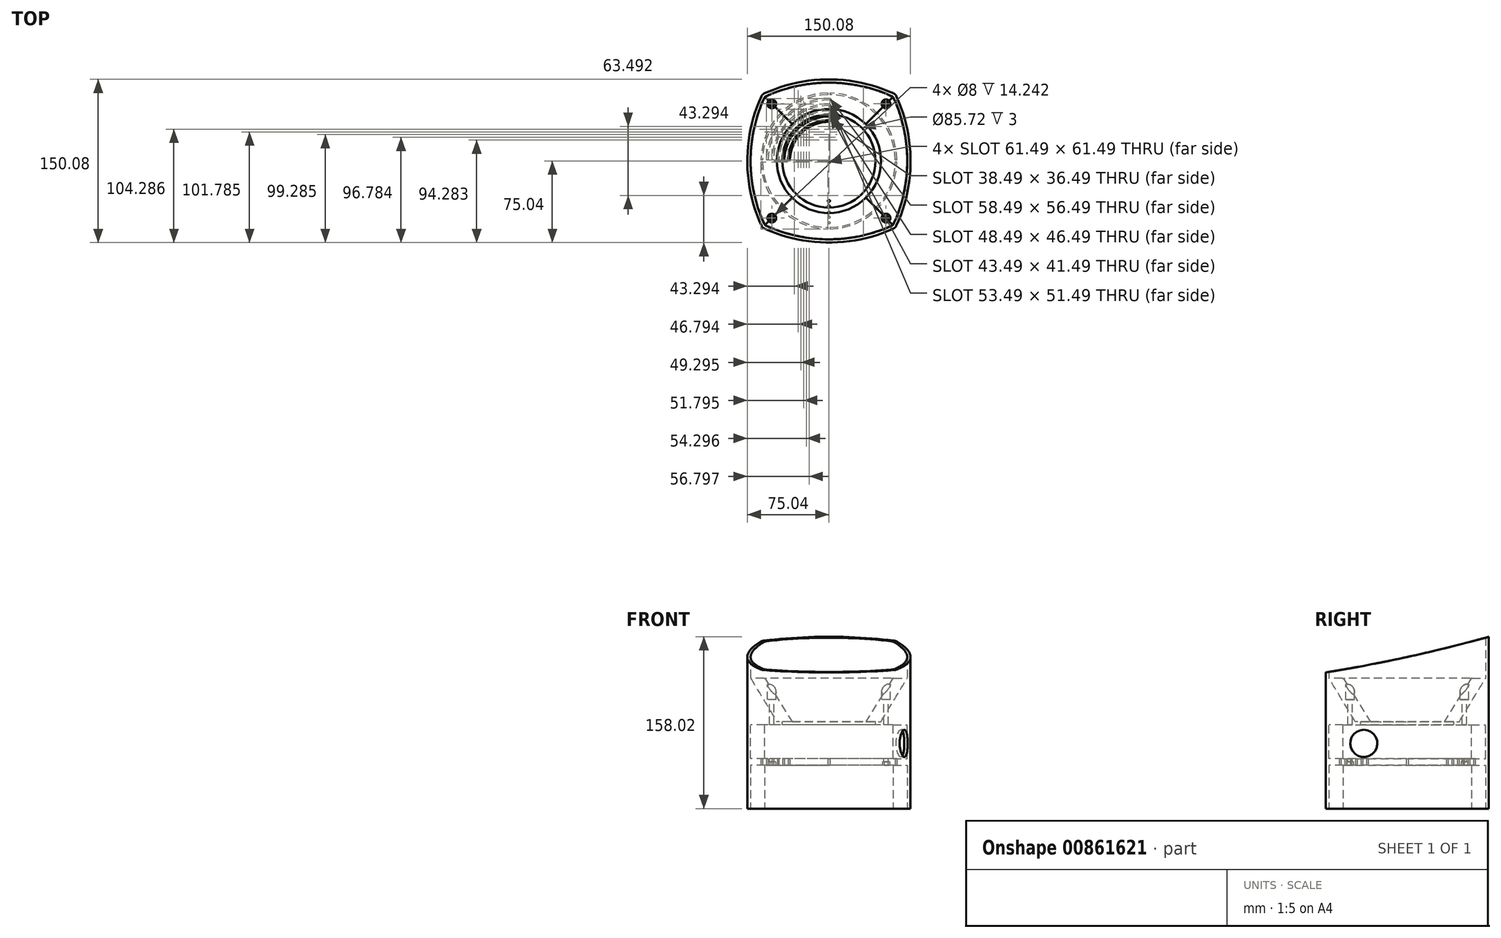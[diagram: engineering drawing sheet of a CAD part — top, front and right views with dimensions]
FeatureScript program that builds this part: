
annotation { "Feature Type Name" : "Feature", "Feature Type Description" : "" }
export const myFeature = defineFeature(function(context is Context, id is Id, definition is map)
    precondition{}
    {
        {
            var Q0;
            Q0=qCreatedBy(makeId("Top.planeOp"),FACE);
            var sketch = newSketch(context, id + "F0", { "sketchPlane" : qUnion([Q0])});
            skLineSegment(sketch, "E0.bottom", {"start": v(196, 49) * mm, "end": v(-196, 49) * mm, "construction": true});
            skLineSegment(sketch, "E0.top", {"start": v(196, -49) * mm, "end": v(-196, -49) * mm, "construction": true});
            skLineSegment(sketch, "E0.left", {"start": v(196, 49) * mm, "end": v(196, -49) * mm, "construction": true});
            skLineSegment(sketch, "E0.right", {"start": v(-196, 49) * mm, "end": v(-196, -49) * mm, "construction": true});
            skPoint(sketch, "E0.middle", {"position": v(0, 0) * mm});
            skLineSegment(sketch, "E1.bottom", {"start": v(207, 59) * mm, "end": v(-207, 59) * mm, "construction": true});
            skLineSegment(sketch, "E1.top", {"start": v(207, -59) * mm, "end": v(-207, -59) * mm, "construction": true});
            skLineSegment(sketch, "E1.left", {"start": v(207, 59) * mm, "end": v(207, -59) * mm, "construction": true});
            skLineSegment(sketch, "E1.right", {"start": v(-207, 59) * mm, "end": v(-207, -59) * mm, "construction": true});
            skLineSegment(sketch, "E2", {"start": v(0, -59) * mm, "end": v(0, 59) * mm, "construction": true});
            skLineSegment(sketch, "E3", {"start": v(-207, 0) * mm, "end": v(207, 0) * mm, "construction": true});
            skCircle(sketch, "E4", {"center": v(0, 0) * mm, "radius": 47.86 * mm});
            skLineSegment(sketch, "E5.bottom", {"start": v(59, 59) * mm, "end": v(-59, 59) * mm, "construction": true});
            skLineSegment(sketch, "E5.top", {"start": v(59, -59) * mm, "end": v(-59, -59) * mm, "construction": true});
            skLineSegment(sketch, "E5.left", {"start": v(59, 59) * mm, "end": v(59, -59) * mm, "construction": true});
            skLineSegment(sketch, "E5.right", {"start": v(-59, 59) * mm, "end": v(-59, -59) * mm, "construction": true});
            skArc(sketch, "E6", {"start": v(59, 59) * mm, "mid": v(0, 72.04) * mm, "end": v(-59, 59) * mm});
            skArc(sketch, "E7", {"start": v(59, -59) * mm, "mid": v(72.04, 0) * mm, "end": v(59, 59) * mm});
            skArc(sketch, "E8", {"start": v(-59, -59) * mm, "mid": v(0, -72.04) * mm, "end": v(59, -59) * mm});
            skArc(sketch, "E9", {"start": v(-59, 59) * mm, "mid": v(-72.04, 0) * mm, "end": v(-59, -59) * mm});
            skArc(sketch, "E10.0", {"start": v(61.26, 61.26) * mm, "mid": v(0, 75.04) * mm, "end": v(-61.26, 61.26) * mm});
            skArc(sketch, "E10.1", {"start": v(61.26, -61.26) * mm, "mid": v(75.04, 0) * mm, "end": v(61.26, 61.26) * mm});
            skArc(sketch, "E10.2", {"start": v(-61.26, -61.26) * mm, "mid": v(0, -75.04) * mm, "end": v(61.26, -61.26) * mm});
            skArc(sketch, "E10.3", {"start": v(-61.26, 61.26) * mm, "mid": v(-75.04, 0) * mm, "end": v(-61.26, -61.26) * mm});
            skSolve(sketch);
        }
        {
            var Q0;
            {var subQ8=sQuery(id+"F0.wireOp",EDGE,"E6");Q0=makeQuery(id+"F0.imprint","IMPRINT",FACE,{"disambiguationData":[TD([[makeQuery(id+"F0.imprint","IMPRINT",EDGE,{"derivedFrom":subQ8}),-1.0]])]});}
            var Q1;
            {var subQ0=sQuery(id+"F0.wireOp",EDGE,"E10.1");var subQ1=sQuery(id+"F0.wireOp",EDGE,"2c3d49d2-39e6-4b7c-b00d-7af9e24e8e71.0");var subQ2=makeQuery(id+"F0.imprint","INTERSECT",VERTEX,{"disambiguationData":[OD(0.0)],"derivedFrom":[subQ1,subQ0]});Q1=makeQuery(id+"F0.imprint","IMPRINT",FACE,{"disambiguationData":[TD([[makeQuery(id+"F0.imprint","IMPRINT",EDGE,{"disambiguationData":[TD([[subQ2,-1.0]])],"derivedFrom":subQ1}),1.0]])]});}
            extrude(context, id + "F1", {"entities" : qUnion([Q0, Q1]), "endBound" : BoundingType.SYMMETRIC, "depth" : 160 * mm, "offsetDistance" : 25 * mm});
        }
        {
            var Q0;
            Q0=qCreatedBy(makeId("Right.planeOp"),FACE);
            var sketch = newSketch(context, id + "F2", { "sketchPlane" : qUnion([Q0])});
            skCircle(sketch, "E11", {"center": v(-294.04, 1407.06) * mm, "radius": 1379.34 * mm});
            skLineSegment(sketch, "E12", {"start": v(0, 0) * mm, "end": v(-237.77, 0) * mm, "construction": true});
            skCircle(sketch, "E13.MirrorC", {"center": v(-294.04, -1407.06) * mm, "radius": 1379.34 * mm});
            skSolve(sketch);
        }
        {
            var Q0;
            Q0=makeQuery(id+"F2.imprint","IMPRINT",FACE,{"disambiguationData":[TD([[makeQuery(id+"F2.imprint","IMPRINT",EDGE,{"derivedFrom":sQuery(id+"F2.wireOp",EDGE,"E11")}),1.0]])]});
            var Q1;
            Q1=makeQuery(id+"F2.imprint","IMPRINT",FACE,{"disambiguationData":[TD([[makeQuery(id+"F2.imprint","IMPRINT",EDGE,{"derivedFrom":sQuery(id+"F2.wireOp",EDGE,"E13.MirrorC")}),-1.0]])]});
            extrude(context, id + "F3", {"entities" : qUnion([Q0, Q1]), "operationType" : NewBodyOperationType.REMOVE, "endBound" : BoundingType.SYMMETRIC, "oppositeDirection" : true, "depth" : 780 * mm, "offsetDistance" : 25 * mm});
        }
        {
            var Q0;
            Q0=qCreatedBy(makeId("Top.planeOp"),FACE);
            cPlane(context, id + "F4", {"entities" : qUnion([Q0]), "cplaneType" : CPlaneType.OFFSET, "offset" : 40 * mm, "width" : 150 * mm, "height" : 150 * mm});
        }
        {
            var Q0;
            Q0=qCreatedBy(id+"F4.planeOp",FACE);
            var sketch = newSketch(context, id + "F5", { "sketchPlane" : qUnion([Q0])});
            skLineSegment(sketch, "E14.bottom", {"start": v(59, 59) * mm, "end": v(-59, 59) * mm, "construction": true});
            skLineSegment(sketch, "E14.top", {"start": v(59, -59) * mm, "end": v(-59, -59) * mm, "construction": true});
            skLineSegment(sketch, "E14.left", {"start": v(59, 59) * mm, "end": v(59, -59) * mm, "construction": true});
            skLineSegment(sketch, "E14.right", {"start": v(-59, 59) * mm, "end": v(-59, -59) * mm, "construction": true});
            skPoint(sketch, "E14.middle", {"position": v(0, 0) * mm});
            skArc(sketch, "E15", {"start": v(59, 59) * mm, "mid": v(0, 72.04) * mm, "end": v(-59, 59) * mm});
            skArc(sketch, "E16", {"start": v(59, -59) * mm, "mid": v(72.04, 0) * mm, "end": v(59, 59) * mm});
            skArc(sketch, "E17", {"start": v(-59, -59) * mm, "mid": v(0, -72.04) * mm, "end": v(59, -59) * mm});
            skArc(sketch, "E18", {"start": v(-59, 59) * mm, "mid": v(-72.04, 0) * mm, "end": v(-59, -59) * mm});
            skSolve(sketch);
        }
        {
            var Q0;
            Q0=qCreatedBy(makeId("Top.planeOp"),FACE);
            var sketch = newSketch(context, id + "F6", { "sketchPlane" : qUnion([Q0])});
            skLineSegment(sketch, "E19.bottom", {"start": v(59, 59) * mm, "end": v(-59, 59) * mm, "construction": true});
            skLineSegment(sketch, "E19.top", {"start": v(59, -59) * mm, "end": v(-59, -59) * mm, "construction": true});
            skLineSegment(sketch, "E19.left", {"start": v(59, 59) * mm, "end": v(59, -59) * mm, "construction": true});
            skLineSegment(sketch, "E19.right", {"start": v(-59, 59) * mm, "end": v(-59, -59) * mm, "construction": true});
            skPoint(sketch, "E19.middle", {"position": v(0, 0) * mm});
            skArc(sketch, "E20", {"start": v(59, 59) * mm, "mid": v(0, 72.04) * mm, "end": v(-59, 59) * mm});
            skArc(sketch, "E21", {"start": v(59, -59) * mm, "mid": v(72.04, 0) * mm, "end": v(59, 59) * mm});
            skArc(sketch, "E22", {"start": v(-59, -59) * mm, "mid": v(0, -72.04) * mm, "end": v(59, -59) * mm});
            skArc(sketch, "E23", {"start": v(-59, 59) * mm, "mid": v(-72.04, 0) * mm, "end": v(-59, -59) * mm});
            skArc(sketch, "E24.0", {"start": v(61.26, 61.26) * mm, "mid": v(0, 75.04) * mm, "end": v(-61.26, 61.26) * mm});
            skArc(sketch, "E24.1", {"start": v(61.26, -61.26) * mm, "mid": v(75.04, 0) * mm, "end": v(61.26, 61.26) * mm});
            skArc(sketch, "E24.2", {"start": v(-61.26, -61.26) * mm, "mid": v(0, -75.04) * mm, "end": v(61.26, -61.26) * mm});
            skArc(sketch, "E24.3", {"start": v(-61.26, 61.26) * mm, "mid": v(-75.04, 0) * mm, "end": v(-61.26, -61.26) * mm});
            skSolve(sketch);
        }
        {
            var Q0;
            Q0 = qSketchRegion(id + "F6", true);
            var Q1;
            Q1=makeQuery(id+"F0.imprint","IMPRINT",FACE,{"disambiguationData":[TD([[makeQuery(id+"F0.imprint","IMPRINT",EDGE,{"derivedFrom":sQuery(id+"F0.wireOp",EDGE,"E4")}),-1.0]])]});
            var Q2;
            Q2=makeQuery(id+"F6.imprint","IMPRINT",FACE,{"disambiguationData":[TD([[makeQuery(id+"F6.imprint","IMPRINT",EDGE,{"derivedFrom":sQuery(id+"F6.wireOp",EDGE,"E20")}),1.0]])]});
            extrude(context, id + "F7", {"entities" : qUnion([Q0, Q1, Q2]), "operationType" : NewBodyOperationType.ADD, "endBound" : BoundingType.SYMMETRIC, "depth" : 80 * mm, "offsetDistance" : 25 * mm});
        }
        {
            var Q0;
            Q0=qCreatedBy(makeId("Top.planeOp"),FACE);
            var sketch = newSketch(context, id + "F8", { "sketchPlane" : qUnion([Q0])});
            skCircle(sketch, "E25", {"center": v(0, 0) * mm, "radius": 47.86 * mm});
            skSolve(sketch);
        }
        {
            var Q1;
            Q1 = qSketchRegion(id + "F5", true);
            var Q2;
            Q2 = qSketchRegion(id + "F8", true);
            loft(context, id + "F9", {"operationType" : NewBodyOperationType.REMOVE, "sheetProfilesArray" : [{ "sheetProfileEntities" : qUnion([Q1]) }, { "sheetProfileEntities" : qUnion([Q2]) }]});
        }
        {
            var Q0;
            Q0=makeQuery(id+"F0.imprint","IMPRINT",FACE,{"disambiguationData":[TD([[makeQuery(id+"F0.imprint","IMPRINT",EDGE,{"derivedFrom":sQuery(id+"F0.wireOp",EDGE,"E4")}),1.0]])]});
            var sketch = newSketch(context, id + "F10", { "sketchPlane" : qUnion([Q0])});
            skCircle(sketch, "E26", {"center": v(0, 0) * mm, "radius": 42.86 * mm});
            skSolve(sketch);
        }
        {
            var Q0;
            Q0=makeQuery(id+"F10.imprint","IMPRINT",FACE,{"disambiguationData":[TD([[makeQuery(id+"F10.imprint","IMPRINT",EDGE,{"derivedFrom":sQuery(id+"F10.wireOp",EDGE,"E26")}),1.0]])]});
            extrude(context, id + "F11", {"entities" : qUnion([Q0]), "operationType" : NewBodyOperationType.REMOVE, "oppositeDirection" : true, "depth" : 3 * mm, "offsetDistance" : 25 * mm});
        }
        {
            var Q0;
            Q0=qCreatedBy(makeId("Top.planeOp"),FACE);
            cPlane(context, id + "F12", {"entities" : qUnion([Q0]), "cplaneType" : CPlaneType.OFFSET, "offset" : 3 * mm, "oppositeDirection" : true, "width" : 150 * mm, "height" : 150 * mm});
        }
        {
            var Q0;
            Q0=qCreatedBy(id+"F12.planeOp",FACE);
            var sketch = newSketch(context, id + "F13", { "sketchPlane" : qUnion([Q0])});
            skLineSegment(sketch, "E27.bottom", {"start": v(59, 59) * mm, "end": v(-59, 59) * mm, "construction": true});
            skLineSegment(sketch, "E27.top", {"start": v(59, -59) * mm, "end": v(-59, -59) * mm, "construction": true});
            skLineSegment(sketch, "E27.left", {"start": v(59, 59) * mm, "end": v(59, -59) * mm, "construction": true});
            skLineSegment(sketch, "E27.right", {"start": v(-59, 59) * mm, "end": v(-59, -59) * mm, "construction": true});
            skPoint(sketch, "E27.middle", {"position": v(0, 0) * mm});
            skArc(sketch, "E28", {"start": v(59, 59) * mm, "mid": v(0, 72.04) * mm, "end": v(-59, 59) * mm});
            skArc(sketch, "E29", {"start": v(59, -59) * mm, "mid": v(72.04, 0) * mm, "end": v(59, 59) * mm});
            skArc(sketch, "E30", {"start": v(-59, -59) * mm, "mid": v(0, -72.04) * mm, "end": v(59, -59) * mm});
            skArc(sketch, "E31", {"start": v(-59, 59) * mm, "mid": v(-72.04, 0) * mm, "end": v(-59, -59) * mm});
            skSolve(sketch);
        }
        {
            var Q0;
            Q0 = qSketchRegion(id + "F13", true);
            extrude(context, id + "F14", {"entities" : qUnion([Q0]), "operationType" : NewBodyOperationType.REMOVE, "oppositeDirection" : true, "depth" : 31 * mm, "offsetDistance" : 25 * mm});
        }
        {
            var Q0;
            Q0=makeQuery(id+"F7.boolean.opBoolean","MERGE",FACE,{"derivedFrom":[makeQuery(id+"F7.opExtrude","CAP_FACE",FACE,{"disambiguationData":[OSD([sQuery(id+"F0.wireOp",EDGE,"E4"),sQuery(id+"F0.wireOp",EDGE,"E6"),sQuery(id+"F0.wireOp",EDGE,"E7"),sQuery(id+"F0.wireOp",EDGE,"E8"),sQuery(id+"F0.wireOp",EDGE,"E9")])],"isStart":true}),makeQuery(id+"F7.opExtrude","CAP_FACE",FACE,{"disambiguationData":[OSD([sQuery(id+"F6.wireOp",EDGE,"E24.0"),sQuery(id+"F6.wireOp",EDGE,"E24.1"),sQuery(id+"F6.wireOp",EDGE,"E24.2"),sQuery(id+"F6.wireOp",EDGE,"E24.3")])],"isStart":true})]});
            var sketch = newSketch(context, id + "F15", { "sketchPlane" : qUnion([Q0])});
            skCircle(sketch, "E32", {"center": v(0, 0) * mm, "radius": 62.5 * mm});
            skCircle(sketch, "E33", {"center": v(0, 0) * mm, "radius": 61 * mm});
            skCircle(sketch, "E34", {"center": v(0, 0) * mm, "radius": 57.5 * mm});
            skCircle(sketch, "E35", {"center": v(0, 0) * mm, "radius": 56 * mm});
            skCircle(sketch, "E36", {"center": v(0, 0) * mm, "radius": 52.5 * mm});
            skCircle(sketch, "E37", {"center": v(0, 0) * mm, "radius": 51 * mm});
            skCircle(sketch, "E38", {"center": v(0, 0) * mm, "radius": 47.5 * mm});
            skCircle(sketch, "E39", {"center": v(0, 0) * mm, "radius": 46 * mm});
            skCircle(sketch, "E40", {"center": v(0, 0) * mm, "radius": 42.5 * mm});
            skCircle(sketch, "E41", {"center": v(0, 0) * mm, "radius": 41 * mm});
            skCircle(sketch, "E42", {"center": v(0, 0) * mm, "radius": 37.5 * mm});
            skCircle(sketch, "E43", {"center": v(0, 0) * mm, "radius": 36 * mm});
            skLineSegment(sketch, "E44.bottom", {"start": v(1, -67) * mm, "end": v(-1, -67) * mm});
            skLineSegment(sketch, "E44.top", {"start": v(1, 67) * mm, "end": v(-1, 67) * mm});
            skLineSegment(sketch, "E44.left", {"start": v(1, -67) * mm, "end": v(1, 67) * mm});
            skLineSegment(sketch, "E44.right", {"start": v(-1, -67) * mm, "end": v(-1, 67) * mm});
            skLineSegment(sketch, "E45.bottom", {"start": v(67.5, -1) * mm, "end": v(-67.5, -1) * mm});
            skLineSegment(sketch, "E45.top", {"start": v(67.5, 1) * mm, "end": v(-67.5, 1) * mm});
            skLineSegment(sketch, "E45.left", {"start": v(67.5, -1) * mm, "end": v(67.5, 1) * mm});
            skLineSegment(sketch, "E45.right", {"start": v(-67.5, -1) * mm, "end": v(-67.5, 1) * mm});
            skSolve(sketch);
        }
        {
            var Q0;
            {var subQ0=sQuery(id+"F15.wireOp",EDGE,"E44.right");var subQ1=sQuery(id+"F15.wireOp",EDGE,"E32");var subQ2=makeQuery(id+"F15.imprint","INTERSECT",VERTEX,{"disambiguationData":[OD(0.0)],"derivedFrom":[subQ1,subQ0]});Q0=makeQuery(id+"F15.imprint","IMPRINT",FACE,{"disambiguationData":[TD([[makeQuery(id+"F15.imprint","IMPRINT",EDGE,{"disambiguationData":[TD([[subQ2,-1.0]])],"derivedFrom":subQ1}),1.0]])]});}
            var Q1;
            {var subQ0=sQuery(id+"F15.wireOp",EDGE,"E44.right");var subQ1=sQuery(id+"F15.wireOp",EDGE,"E34");var subQ2=makeQuery(id+"F15.imprint","INTERSECT",VERTEX,{"disambiguationData":[OD(0.0)],"derivedFrom":[subQ1,subQ0]});Q1=makeQuery(id+"F15.imprint","IMPRINT",FACE,{"disambiguationData":[TD([[makeQuery(id+"F15.imprint","IMPRINT",EDGE,{"disambiguationData":[TD([[subQ2,-1.0]])],"derivedFrom":subQ1}),1.0]])]});}
            var Q2;
            {var subQ0=sQuery(id+"F15.wireOp",EDGE,"E44.right");var subQ1=sQuery(id+"F15.wireOp",EDGE,"E36");var subQ2=makeQuery(id+"F15.imprint","INTERSECT",VERTEX,{"disambiguationData":[OD(0.0)],"derivedFrom":[subQ1,subQ0]});Q2=makeQuery(id+"F15.imprint","IMPRINT",FACE,{"disambiguationData":[TD([[makeQuery(id+"F15.imprint","IMPRINT",EDGE,{"disambiguationData":[TD([[subQ2,-1.0]])],"derivedFrom":subQ1}),1.0]])]});}
            var Q3;
            {var subQ0=sQuery(id+"F15.wireOp",EDGE,"E44.right");var subQ1=sQuery(id+"F15.wireOp",EDGE,"E38");var subQ2=makeQuery(id+"F15.imprint","INTERSECT",VERTEX,{"disambiguationData":[OD(0.0)],"derivedFrom":[subQ1,subQ0]});Q3=makeQuery(id+"F15.imprint","IMPRINT",FACE,{"disambiguationData":[TD([[makeQuery(id+"F15.imprint","IMPRINT",EDGE,{"disambiguationData":[TD([[subQ2,-1.0]])],"derivedFrom":subQ1}),1.0]])]});}
            var Q4;
            {var subQ0=sQuery(id+"F15.wireOp",EDGE,"E44.right");var subQ1=sQuery(id+"F15.wireOp",EDGE,"E40");var subQ2=makeQuery(id+"F15.imprint","INTERSECT",VERTEX,{"disambiguationData":[OD(0.0)],"derivedFrom":[subQ1,subQ0]});Q4=makeQuery(id+"F15.imprint","IMPRINT",FACE,{"disambiguationData":[TD([[makeQuery(id+"F15.imprint","IMPRINT",EDGE,{"disambiguationData":[TD([[subQ2,-1.0]])],"derivedFrom":subQ1}),1.0]])]});}
            var Q5;
            {var subQ0=sQuery(id+"F15.wireOp",EDGE,"E44.right");var subQ1=sQuery(id+"F15.wireOp",EDGE,"E42");var subQ2=makeQuery(id+"F15.imprint","INTERSECT",VERTEX,{"disambiguationData":[OD(0.0)],"derivedFrom":[subQ1,subQ0]});Q5=makeQuery(id+"F15.imprint","IMPRINT",FACE,{"disambiguationData":[TD([[makeQuery(id+"F15.imprint","IMPRINT",EDGE,{"disambiguationData":[TD([[subQ2,-1.0]])],"derivedFrom":subQ1}),1.0]])]});}
            var Q6;
            {var subQ0=sQuery(id+"F15.wireOp",EDGE,"E44.left");var subQ1=sQuery(id+"F15.wireOp",EDGE,"E42");var subQ2=makeQuery(id+"F15.imprint","INTERSECT",VERTEX,{"disambiguationData":[OD(0.0)],"derivedFrom":[subQ1,subQ0]});Q6=makeQuery(id+"F15.imprint","IMPRINT",FACE,{"disambiguationData":[TD([[makeQuery(id+"F15.imprint","IMPRINT",EDGE,{"disambiguationData":[TD([[subQ2,1.0]])],"derivedFrom":subQ1}),1.0]])]});}
            var Q7;
            {var subQ0=sQuery(id+"F15.wireOp",EDGE,"E44.left");var subQ1=sQuery(id+"F15.wireOp",EDGE,"E40");var subQ2=makeQuery(id+"F15.imprint","INTERSECT",VERTEX,{"disambiguationData":[OD(0.0)],"derivedFrom":[subQ1,subQ0]});Q7=makeQuery(id+"F15.imprint","IMPRINT",FACE,{"disambiguationData":[TD([[makeQuery(id+"F15.imprint","IMPRINT",EDGE,{"disambiguationData":[TD([[subQ2,1.0]])],"derivedFrom":subQ1}),1.0]])]});}
            var Q8;
            {var subQ0=sQuery(id+"F15.wireOp",EDGE,"E44.left");var subQ1=sQuery(id+"F15.wireOp",EDGE,"E38");var subQ2=makeQuery(id+"F15.imprint","INTERSECT",VERTEX,{"disambiguationData":[OD(0.0)],"derivedFrom":[subQ1,subQ0]});Q8=makeQuery(id+"F15.imprint","IMPRINT",FACE,{"disambiguationData":[TD([[makeQuery(id+"F15.imprint","IMPRINT",EDGE,{"disambiguationData":[TD([[subQ2,1.0]])],"derivedFrom":subQ1}),1.0]])]});}
            var Q9;
            {var subQ0=sQuery(id+"F15.wireOp",EDGE,"E44.left");var subQ1=sQuery(id+"F15.wireOp",EDGE,"E36");var subQ2=makeQuery(id+"F15.imprint","INTERSECT",VERTEX,{"disambiguationData":[OD(0.0)],"derivedFrom":[subQ1,subQ0]});Q9=makeQuery(id+"F15.imprint","IMPRINT",FACE,{"disambiguationData":[TD([[makeQuery(id+"F15.imprint","IMPRINT",EDGE,{"disambiguationData":[TD([[subQ2,1.0]])],"derivedFrom":subQ1}),1.0]])]});}
            var Q10;
            {var subQ0=sQuery(id+"F15.wireOp",EDGE,"E44.left");var subQ1=sQuery(id+"F15.wireOp",EDGE,"E34");var subQ2=makeQuery(id+"F15.imprint","INTERSECT",VERTEX,{"disambiguationData":[OD(0.0)],"derivedFrom":[subQ1,subQ0]});Q10=makeQuery(id+"F15.imprint","IMPRINT",FACE,{"disambiguationData":[TD([[makeQuery(id+"F15.imprint","IMPRINT",EDGE,{"disambiguationData":[TD([[subQ2,1.0]])],"derivedFrom":subQ1}),1.0]])]});}
            var Q11;
            {var subQ0=sQuery(id+"F15.wireOp",EDGE,"E44.left");var subQ1=sQuery(id+"F15.wireOp",EDGE,"E32");var subQ2=makeQuery(id+"F15.imprint","INTERSECT",VERTEX,{"disambiguationData":[OD(0.0)],"derivedFrom":[subQ1,subQ0]});Q11=makeQuery(id+"F15.imprint","IMPRINT",FACE,{"disambiguationData":[TD([[makeQuery(id+"F15.imprint","IMPRINT",EDGE,{"disambiguationData":[TD([[subQ2,1.0]])],"derivedFrom":subQ1}),1.0]])]});}
            var Q12;
            {var subQ0=sQuery(id+"F15.wireOp",EDGE,"E44.left");var subQ1=sQuery(id+"F15.wireOp",EDGE,"E42");var subQ2=makeQuery(id+"F15.imprint","INTERSECT",VERTEX,{"disambiguationData":[OD(1.0)],"derivedFrom":[subQ1,subQ0]});Q12=makeQuery(id+"F15.imprint","IMPRINT",FACE,{"disambiguationData":[TD([[makeQuery(id+"F15.imprint","IMPRINT",EDGE,{"disambiguationData":[TD([[subQ2,-1.0]])],"derivedFrom":subQ1}),1.0]])]});}
            var Q13;
            {var subQ0=sQuery(id+"F15.wireOp",EDGE,"E45.bottom");var subQ1=sQuery(id+"F15.wireOp",EDGE,"E42");var subQ2=makeQuery(id+"F15.imprint","INTERSECT",VERTEX,{"disambiguationData":[OD(0.0)],"derivedFrom":[subQ1,subQ0]});Q13=makeQuery(id+"F15.imprint","IMPRINT",FACE,{"disambiguationData":[TD([[makeQuery(id+"F15.imprint","IMPRINT",EDGE,{"disambiguationData":[TD([[subQ2,-1.0]])],"derivedFrom":subQ1}),1.0]])]});}
            var Q14;
            {var subQ0=sQuery(id+"F15.wireOp",EDGE,"E45.bottom");var subQ1=sQuery(id+"F15.wireOp",EDGE,"E40");var subQ2=makeQuery(id+"F15.imprint","INTERSECT",VERTEX,{"disambiguationData":[OD(0.0)],"derivedFrom":[subQ1,subQ0]});Q14=makeQuery(id+"F15.imprint","IMPRINT",FACE,{"disambiguationData":[TD([[makeQuery(id+"F15.imprint","IMPRINT",EDGE,{"disambiguationData":[TD([[subQ2,-1.0]])],"derivedFrom":subQ1}),1.0]])]});}
            var Q15;
            {var subQ0=sQuery(id+"F15.wireOp",EDGE,"E44.left");var subQ1=sQuery(id+"F15.wireOp",EDGE,"E40");var subQ2=makeQuery(id+"F15.imprint","INTERSECT",VERTEX,{"disambiguationData":[OD(1.0)],"derivedFrom":[subQ1,subQ0]});Q15=makeQuery(id+"F15.imprint","IMPRINT",FACE,{"disambiguationData":[TD([[makeQuery(id+"F15.imprint","IMPRINT",EDGE,{"disambiguationData":[TD([[subQ2,-1.0]])],"derivedFrom":subQ1}),1.0]])]});}
            var Q16;
            {var subQ0=sQuery(id+"F15.wireOp",EDGE,"E44.left");var subQ1=sQuery(id+"F15.wireOp",EDGE,"E38");var subQ2=makeQuery(id+"F15.imprint","INTERSECT",VERTEX,{"disambiguationData":[OD(1.0)],"derivedFrom":[subQ1,subQ0]});Q16=makeQuery(id+"F15.imprint","IMPRINT",FACE,{"disambiguationData":[TD([[makeQuery(id+"F15.imprint","IMPRINT",EDGE,{"disambiguationData":[TD([[subQ2,-1.0]])],"derivedFrom":subQ1}),1.0]])]});}
            var Q17;
            {var subQ0=sQuery(id+"F15.wireOp",EDGE,"E45.bottom");var subQ1=sQuery(id+"F15.wireOp",EDGE,"E38");var subQ2=makeQuery(id+"F15.imprint","INTERSECT",VERTEX,{"disambiguationData":[OD(0.0)],"derivedFrom":[subQ1,subQ0]});Q17=makeQuery(id+"F15.imprint","IMPRINT",FACE,{"disambiguationData":[TD([[makeQuery(id+"F15.imprint","IMPRINT",EDGE,{"disambiguationData":[TD([[subQ2,-1.0]])],"derivedFrom":subQ1}),1.0]])]});}
            var Q18;
            {var subQ0=sQuery(id+"F15.wireOp",EDGE,"E45.bottom");var subQ1=sQuery(id+"F15.wireOp",EDGE,"E36");var subQ2=makeQuery(id+"F15.imprint","INTERSECT",VERTEX,{"disambiguationData":[OD(0.0)],"derivedFrom":[subQ1,subQ0]});Q18=makeQuery(id+"F15.imprint","IMPRINT",FACE,{"disambiguationData":[TD([[makeQuery(id+"F15.imprint","IMPRINT",EDGE,{"disambiguationData":[TD([[subQ2,-1.0]])],"derivedFrom":subQ1}),1.0]])]});}
            var Q19;
            {var subQ0=sQuery(id+"F15.wireOp",EDGE,"E44.left");var subQ1=sQuery(id+"F15.wireOp",EDGE,"E36");var subQ2=makeQuery(id+"F15.imprint","INTERSECT",VERTEX,{"disambiguationData":[OD(1.0)],"derivedFrom":[subQ1,subQ0]});Q19=makeQuery(id+"F15.imprint","IMPRINT",FACE,{"disambiguationData":[TD([[makeQuery(id+"F15.imprint","IMPRINT",EDGE,{"disambiguationData":[TD([[subQ2,-1.0]])],"derivedFrom":subQ1}),1.0]])]});}
            var Q20;
            {var subQ0=sQuery(id+"F15.wireOp",EDGE,"E44.left");var subQ1=sQuery(id+"F15.wireOp",EDGE,"E34");var subQ2=makeQuery(id+"F15.imprint","INTERSECT",VERTEX,{"disambiguationData":[OD(1.0)],"derivedFrom":[subQ1,subQ0]});Q20=makeQuery(id+"F15.imprint","IMPRINT",FACE,{"disambiguationData":[TD([[makeQuery(id+"F15.imprint","IMPRINT",EDGE,{"disambiguationData":[TD([[subQ2,-1.0]])],"derivedFrom":subQ1}),1.0]])]});}
            var Q21;
            {var subQ0=sQuery(id+"F15.wireOp",EDGE,"E45.bottom");var subQ1=sQuery(id+"F15.wireOp",EDGE,"E34");var subQ2=makeQuery(id+"F15.imprint","INTERSECT",VERTEX,{"disambiguationData":[OD(0.0)],"derivedFrom":[subQ1,subQ0]});Q21=makeQuery(id+"F15.imprint","IMPRINT",FACE,{"disambiguationData":[TD([[makeQuery(id+"F15.imprint","IMPRINT",EDGE,{"disambiguationData":[TD([[subQ2,-1.0]])],"derivedFrom":subQ1}),1.0]])]});}
            var Q22;
            {var subQ0=sQuery(id+"F15.wireOp",EDGE,"E45.bottom");var subQ1=sQuery(id+"F15.wireOp",EDGE,"E32");var subQ2=makeQuery(id+"F15.imprint","INTERSECT",VERTEX,{"disambiguationData":[OD(0.0)],"derivedFrom":[subQ1,subQ0]});Q22=makeQuery(id+"F15.imprint","IMPRINT",FACE,{"disambiguationData":[TD([[makeQuery(id+"F15.imprint","IMPRINT",EDGE,{"disambiguationData":[TD([[subQ2,-1.0]])],"derivedFrom":subQ1}),1.0]])]});}
            var Q23;
            {var subQ0=sQuery(id+"F15.wireOp",EDGE,"E44.left");var subQ1=sQuery(id+"F15.wireOp",EDGE,"E32");var subQ2=makeQuery(id+"F15.imprint","INTERSECT",VERTEX,{"disambiguationData":[OD(1.0)],"derivedFrom":[subQ1,subQ0]});Q23=makeQuery(id+"F15.imprint","IMPRINT",FACE,{"disambiguationData":[TD([[makeQuery(id+"F15.imprint","IMPRINT",EDGE,{"disambiguationData":[TD([[subQ2,-1.0]])],"derivedFrom":subQ1}),1.0]])]});}
            extrude(context, id + "F16", {"entities" : qUnion([Q0, Q1, Q2, Q3, Q4, Q5, Q6, Q7, Q8, Q9, Q10, Q11, Q12, Q13, Q14, Q15, Q16, Q17, Q18, Q19, Q20, Q21, Q22, Q23]), "operationType" : NewBodyOperationType.REMOVE, "oppositeDirection" : true, "depth" : 25 * mm, "offsetDistance" : 25 * mm});
        }
        {
            var Q0;
            Q0=makeQuery(id+"F1.opExtrude","SWEPT_EDGE",EDGE,{"disambiguationData":[OSD([sQuery(id+"F0.wireOp",EDGE,"E10.0"),sQuery(id+"F0.wireOp",EDGE,"E10.3")])]});
            var Q1;
            Q1=makeQuery(id+"F1.opExtrude","SWEPT_EDGE",EDGE,{"disambiguationData":[OSD([sQuery(id+"F0.wireOp",EDGE,"E10.2"),sQuery(id+"F0.wireOp",EDGE,"E10.3")])]});
            var Q2;
            Q2=makeQuery(id+"F1.opExtrude","SWEPT_EDGE",EDGE,{"disambiguationData":[OSD([sQuery(id+"F0.wireOp",EDGE,"E10.0"),sQuery(id+"F0.wireOp",EDGE,"E10.1")])]});
            var Q3;
            Q3=makeQuery(id+"F1.opExtrude","SWEPT_EDGE",EDGE,{"disambiguationData":[OSD([sQuery(id+"F0.wireOp",EDGE,"E10.1"),sQuery(id+"F0.wireOp",EDGE,"E10.2")])]});
            var Q4;
            {var subQ0=sQuery(id+"F0.wireOp",EDGE,"E9");var subQ1=sQuery(id+"F0.wireOp",EDGE,"E6");Q4=makeQuery(id+"F7.boolean.opBoolean","SPLIT",EDGE,{"disambiguationData":[TD([makeQuery(id+"F3.boolean.opBoolean","COPY",FACE,{"derivedFrom":makeQuery(id+"F3.opExtrude","SWEPT_FACE",FACE,{"disambiguationData":[OSD([sQuery(id+"F2.wireOp",EDGE,"E11")])]})})])],"derivedFrom":makeQuery(id+"F1.opExtrude","SWEPT_EDGE",EDGE,{"disambiguationData":[OSD([subQ1,subQ0])]})});}
            var Q5;
            {var subQ0=sQuery(id+"F0.wireOp",EDGE,"E7");var subQ1=sQuery(id+"F0.wireOp",EDGE,"E6");Q5=makeQuery(id+"F7.boolean.opBoolean","SPLIT",EDGE,{"disambiguationData":[TD([makeQuery(id+"F3.boolean.opBoolean","COPY",FACE,{"derivedFrom":makeQuery(id+"F3.opExtrude","SWEPT_FACE",FACE,{"disambiguationData":[OSD([sQuery(id+"F2.wireOp",EDGE,"E11")])]})})])],"derivedFrom":makeQuery(id+"F1.opExtrude","SWEPT_EDGE",EDGE,{"disambiguationData":[OSD([subQ1,subQ0])]})});}
            var Q6;
            {var subQ0=sQuery(id+"F0.wireOp",EDGE,"E9");var subQ1=sQuery(id+"F0.wireOp",EDGE,"E8");Q6=makeQuery(id+"F7.boolean.opBoolean","SPLIT",EDGE,{"disambiguationData":[TD([makeQuery(id+"F3.boolean.opBoolean","COPY",FACE,{"derivedFrom":makeQuery(id+"F3.opExtrude","SWEPT_FACE",FACE,{"disambiguationData":[OSD([sQuery(id+"F2.wireOp",EDGE,"E11")])]})})])],"derivedFrom":makeQuery(id+"F1.opExtrude","SWEPT_EDGE",EDGE,{"disambiguationData":[OSD([subQ1,subQ0])]})});}
            var Q7;
            {var subQ0=sQuery(id+"F0.wireOp",EDGE,"E8");var subQ1=sQuery(id+"F0.wireOp",EDGE,"E7");Q7=makeQuery(id+"F7.boolean.opBoolean","SPLIT",EDGE,{"disambiguationData":[TD([makeQuery(id+"F3.boolean.opBoolean","COPY",FACE,{"derivedFrom":makeQuery(id+"F3.opExtrude","SWEPT_FACE",FACE,{"disambiguationData":[OSD([sQuery(id+"F2.wireOp",EDGE,"E11")])]})})])],"derivedFrom":makeQuery(id+"F1.opExtrude","SWEPT_EDGE",EDGE,{"disambiguationData":[OSD([subQ1,subQ0])]})});}
            var Q8;
            {var subQ0=sQuery(id+"F0.wireOp",EDGE,"E8");var subQ1=sQuery(id+"F0.wireOp",EDGE,"E7");Q8=makeQuery(id+"F7.boolean.opBoolean","SPLIT",EDGE,{"disambiguationData":[TD([makeQuery(id+"F3.boolean.opBoolean","COPY",FACE,{"derivedFrom":makeQuery(id+"F3.opExtrude","SWEPT_FACE",FACE,{"disambiguationData":[OSD([sQuery(id+"F2.wireOp",EDGE,"E13.MirrorC")])]})})])],"derivedFrom":makeQuery(id+"F1.opExtrude","SWEPT_EDGE",EDGE,{"disambiguationData":[OSD([subQ1,subQ0])]})});}
            var Q9;
            {var subQ0=sQuery(id+"F0.wireOp",EDGE,"E9");var subQ1=sQuery(id+"F0.wireOp",EDGE,"E8");Q9=makeQuery(id+"F7.boolean.opBoolean","SPLIT",EDGE,{"disambiguationData":[TD([makeQuery(id+"F3.boolean.opBoolean","COPY",FACE,{"derivedFrom":makeQuery(id+"F3.opExtrude","SWEPT_FACE",FACE,{"disambiguationData":[OSD([sQuery(id+"F2.wireOp",EDGE,"E13.MirrorC")])]})})])],"derivedFrom":makeQuery(id+"F1.opExtrude","SWEPT_EDGE",EDGE,{"disambiguationData":[OSD([subQ1,subQ0])]})});}
            var Q10;
            {var subQ0=sQuery(id+"F0.wireOp",EDGE,"E9");var subQ1=sQuery(id+"F0.wireOp",EDGE,"E6");Q10=makeQuery(id+"F7.boolean.opBoolean","SPLIT",EDGE,{"disambiguationData":[TD([makeQuery(id+"F3.boolean.opBoolean","COPY",FACE,{"derivedFrom":makeQuery(id+"F3.opExtrude","SWEPT_FACE",FACE,{"disambiguationData":[OSD([sQuery(id+"F2.wireOp",EDGE,"E13.MirrorC")])]})})])],"derivedFrom":makeQuery(id+"F1.opExtrude","SWEPT_EDGE",EDGE,{"disambiguationData":[OSD([subQ1,subQ0])]})});}
            var Q11;
            {var subQ0=sQuery(id+"F0.wireOp",EDGE,"E7");var subQ1=sQuery(id+"F0.wireOp",EDGE,"E6");Q11=makeQuery(id+"F7.boolean.opBoolean","SPLIT",EDGE,{"disambiguationData":[TD([makeQuery(id+"F3.boolean.opBoolean","COPY",FACE,{"derivedFrom":makeQuery(id+"F3.opExtrude","SWEPT_FACE",FACE,{"disambiguationData":[OSD([sQuery(id+"F2.wireOp",EDGE,"E13.MirrorC")])]})})])],"derivedFrom":makeQuery(id+"F1.opExtrude","SWEPT_EDGE",EDGE,{"disambiguationData":[OSD([subQ1,subQ0])]})});}
            fillet(context, id + "F17", {"entities" : qUnion([Q0, Q1, Q2, Q3, Q4, Q5, Q6, Q7, Q8, Q9, Q10, Q11]), "radius" : 5 * mm, "tangentPropagation" : true, "allowEdgeOverflow" : false});
        }
        {
            var Q0;
            Q0=qCreatedBy(makeId("Top.planeOp"),FACE);
            cPlane(context, id + "F18", {"entities" : qUnion([Q0]), "cplaneType" : CPlaneType.OFFSET, "offset" : 50 * mm, "width" : 150 * mm, "height" : 150 * mm});
        }
        {
            var Q0;
            Q0=qCreatedBy(id+"F18.planeOp",FACE);
            var sketch = newSketch(context, id + "F19", { "sketchPlane" : qUnion([Q0])});
            skLineSegment(sketch, "E46.bottom", {"start": v(52.5, 52.5) * mm, "end": v(-52.5, 52.5) * mm, "construction": true});
            skLineSegment(sketch, "E46.top", {"start": v(52.5, -52.5) * mm, "end": v(-52.5, -52.5) * mm, "construction": true});
            skLineSegment(sketch, "E46.left", {"start": v(52.5, 52.5) * mm, "end": v(52.5, -52.5) * mm, "construction": true});
            skLineSegment(sketch, "E46.right", {"start": v(-52.5, 52.5) * mm, "end": v(-52.5, -52.5) * mm, "construction": true});
            skPoint(sketch, "E46.middle", {"position": v(0, 0) * mm});
            skCircle(sketch, "E47", {"center": v(-52.5, 52.5) * mm, "radius": 2 * mm});
            skCircle(sketch, "E48", {"center": v(52.5, 52.5) * mm, "radius": 2 * mm});
            skCircle(sketch, "E49", {"center": v(52.5, -52.5) * mm, "radius": 2 * mm});
            skCircle(sketch, "E50", {"center": v(-52.5, -52.5) * mm, "radius": 2 * mm});
            skSolve(sketch);
        }
        {
            var Q0;
            Q0=sQuery(id+"F19.wireOp",VERTEX,"E46.bottom.end");
            var Q1;
            Q1=sQuery(id+"F19.wireOp",VERTEX,"E46.bottom.start");
            var Q2;
            Q2=sQuery(id+"F19.wireOp",VERTEX,"E46.top.start");
            var Q3;
            Q3=sQuery(id+"F19.wireOp",VERTEX,"E46.top.end");
            var Q4;
            Q4=makeQuery(id+"F1.opExtrude","SWEPT_BODY",BODY,{"disambiguationData":[OSD([sQuery(id+"F0.wireOp",EDGE,"E6"),sQuery(id+"F0.wireOp",EDGE,"E7"),sQuery(id+"F0.wireOp",EDGE,"E8"),sQuery(id+"F0.wireOp",EDGE,"E9"),sQuery(id+"F0.wireOp",EDGE,"E10.0"),sQuery(id+"F0.wireOp",EDGE,"E10.1"),sQuery(id+"F0.wireOp",EDGE,"E10.2"),sQuery(id+"F0.wireOp",EDGE,"E10.3")])]});
            hole(context, id + "F20", {"style" : HoleStyle.C_BORE, "endStyle" : HoleEndStyle.THROUGH, "holeDiameter" : 4 * mm, "cBoreDiameter" : 8 * mm, "cBoreDepth" : 5 * mm, "majorDiameter" : 5 * mm, "isTappedThrough" : true, "tappedDepth" : 12 * mm, "tapClearance" : 3, "locations" : qUnion([Q0, Q1, Q2, Q3]), "scope" : qUnion([Q4])});
        }
        {
            var Q0;
            Q0=makeQuery(id+"F7.boolean.opBoolean","MERGE",FACE,{"derivedFrom":[makeQuery(id+"F7.opExtrude","CAP_FACE",FACE,{"disambiguationData":[OSD([sQuery(id+"F0.wireOp",EDGE,"E4"),sQuery(id+"F0.wireOp",EDGE,"E6"),sQuery(id+"F0.wireOp",EDGE,"E7"),sQuery(id+"F0.wireOp",EDGE,"E8"),sQuery(id+"F0.wireOp",EDGE,"E9")])],"isStart":true}),makeQuery(id+"F7.opExtrude","CAP_FACE",FACE,{"disambiguationData":[OSD([sQuery(id+"F6.wireOp",EDGE,"E24.0"),sQuery(id+"F6.wireOp",EDGE,"E24.1"),sQuery(id+"F6.wireOp",EDGE,"E24.2"),sQuery(id+"F6.wireOp",EDGE,"E24.3")])],"isStart":true})]});
            var sketch = newSketch(context, id + "F21", { "sketchPlane" : qUnion([Q0])});
            skCircle(sketch, "E51.cCircle", {"center": v(-52.5, 52.5) * mm, "radius": 3 * mm, "construction": true});
            skLineSegment(sketch, "E51.0", {"start": v(-54.23, 55.5) * mm, "end": v(-50.77, 55.5) * mm});
            skLineSegment(sketch, "E51.1", {"start": v(-50.77, 55.5) * mm, "end": v(-49.04, 52.5) * mm});
            skLineSegment(sketch, "E51.2", {"start": v(-49.04, 52.5) * mm, "end": v(-50.77, 49.5) * mm});
            skLineSegment(sketch, "E51.3", {"start": v(-50.77, 49.5) * mm, "end": v(-54.23, 49.5) * mm});
            skLineSegment(sketch, "E51.4", {"start": v(-54.23, 49.5) * mm, "end": v(-55.96, 52.5) * mm});
            skLineSegment(sketch, "E51.5", {"start": v(-55.96, 52.5) * mm, "end": v(-54.23, 55.5) * mm});
            skPoint(sketch, "E51.0.midPoint", {"position": v(-52.5, 55.5) * mm});
            skCircle(sketch, "E52.cCircle", {"center": v(52.5, 52.5) * mm, "radius": 3 * mm, "construction": true});
            skLineSegment(sketch, "E52.0", {"start": v(50.77, 55.5) * mm, "end": v(54.23, 55.5) * mm});
            skLineSegment(sketch, "E52.1", {"start": v(54.23, 55.5) * mm, "end": v(55.96, 52.5) * mm});
            skLineSegment(sketch, "E52.2", {"start": v(55.96, 52.5) * mm, "end": v(54.23, 49.5) * mm});
            skLineSegment(sketch, "E52.3", {"start": v(54.23, 49.5) * mm, "end": v(50.77, 49.5) * mm});
            skLineSegment(sketch, "E52.4", {"start": v(50.77, 49.5) * mm, "end": v(49.04, 52.5) * mm});
            skLineSegment(sketch, "E52.5", {"start": v(49.04, 52.5) * mm, "end": v(50.77, 55.5) * mm});
            skPoint(sketch, "E52.0.midPoint", {"position": v(52.5, 55.5) * mm});
            skCircle(sketch, "E53.cCircle", {"center": v(52.5, -52.5) * mm, "radius": 3 * mm, "construction": true});
            skLineSegment(sketch, "E53.0", {"start": v(50.77, -49.5) * mm, "end": v(54.23, -49.5) * mm});
            skLineSegment(sketch, "E53.1", {"start": v(54.23, -49.5) * mm, "end": v(55.96, -52.5) * mm});
            skLineSegment(sketch, "E53.2", {"start": v(55.96, -52.5) * mm, "end": v(54.23, -55.5) * mm});
            skLineSegment(sketch, "E53.3", {"start": v(54.23, -55.5) * mm, "end": v(50.77, -55.5) * mm});
            skLineSegment(sketch, "E53.4", {"start": v(50.77, -55.5) * mm, "end": v(49.04, -52.5) * mm});
            skLineSegment(sketch, "E53.5", {"start": v(49.04, -52.5) * mm, "end": v(50.77, -49.5) * mm});
            skPoint(sketch, "E53.0.midPoint", {"position": v(52.5, -49.5) * mm});
            skCircle(sketch, "E54.cCircle", {"center": v(-52.5, -52.5) * mm, "radius": 3 * mm, "construction": true});
            skLineSegment(sketch, "E54.0", {"start": v(-54.23, -49.5) * mm, "end": v(-50.77, -49.5) * mm});
            skLineSegment(sketch, "E54.1", {"start": v(-50.77, -49.5) * mm, "end": v(-49.04, -52.5) * mm});
            skLineSegment(sketch, "E54.2", {"start": v(-49.04, -52.5) * mm, "end": v(-50.77, -55.5) * mm});
            skLineSegment(sketch, "E54.3", {"start": v(-50.77, -55.5) * mm, "end": v(-54.23, -55.5) * mm});
            skLineSegment(sketch, "E54.4", {"start": v(-54.23, -55.5) * mm, "end": v(-55.96, -52.5) * mm});
            skLineSegment(sketch, "E54.5", {"start": v(-55.96, -52.5) * mm, "end": v(-54.23, -49.5) * mm});
            skPoint(sketch, "E54.0.midPoint", {"position": v(-52.5, -49.5) * mm});
            skSolve(sketch);
        }
        {
            var Q0;
            Q0=makeQuery(id+"F21.imprint","IMPRINT",FACE,{"disambiguationData":[TD([[makeQuery(id+"F21.imprint","IMPRINT",EDGE,{"derivedFrom":sQuery(id+"F21.wireOp",EDGE,"E51.0")}),-1.0]])]});
            var Q1;
            Q1=makeQuery(id+"F21.imprint","IMPRINT",FACE,{"disambiguationData":[TD([[makeQuery(id+"F21.imprint","IMPRINT",EDGE,{"derivedFrom":sQuery(id+"F21.wireOp",EDGE,"E52.0")}),-1.0]])]});
            var Q2;
            Q2=makeQuery(id+"F21.imprint","IMPRINT",FACE,{"disambiguationData":[TD([[makeQuery(id+"F21.imprint","IMPRINT",EDGE,{"derivedFrom":sQuery(id+"F21.wireOp",EDGE,"E53.0")}),-1.0]])]});
            var Q3;
            Q3=makeQuery(id+"F21.imprint","IMPRINT",FACE,{"disambiguationData":[TD([[makeQuery(id+"F21.imprint","IMPRINT",EDGE,{"derivedFrom":sQuery(id+"F21.wireOp",EDGE,"E54.0")}),-1.0]])]});
            extrude(context, id + "F22", {"entities" : qUnion([Q0, Q1, Q2, Q3]), "operationType" : NewBodyOperationType.REMOVE, "oppositeDirection" : true, "depth" : 3 * mm, "offsetDistance" : 25 * mm});
        }
        {
            var Q0;
            Q0=qCreatedBy(makeId("Right.planeOp"),FACE);
            var sketch = newSketch(context, id + "F23", { "sketchPlane" : qUnion([Q0])});
            skCircle(sketch, "E55", {"center": v(-40, -20) * mm, "radius": 12.5 * mm});
            skSolve(sketch);
        }
        {
            var Q0;
            Q0 = qSketchRegion(id + "F23", true);
            extrude(context, id + "F24", {"entities" : qUnion([Q0]), "operationType" : NewBodyOperationType.REMOVE, "depth" : 249 * mm, "offsetDistance" : 25 * mm});
        }
    });
